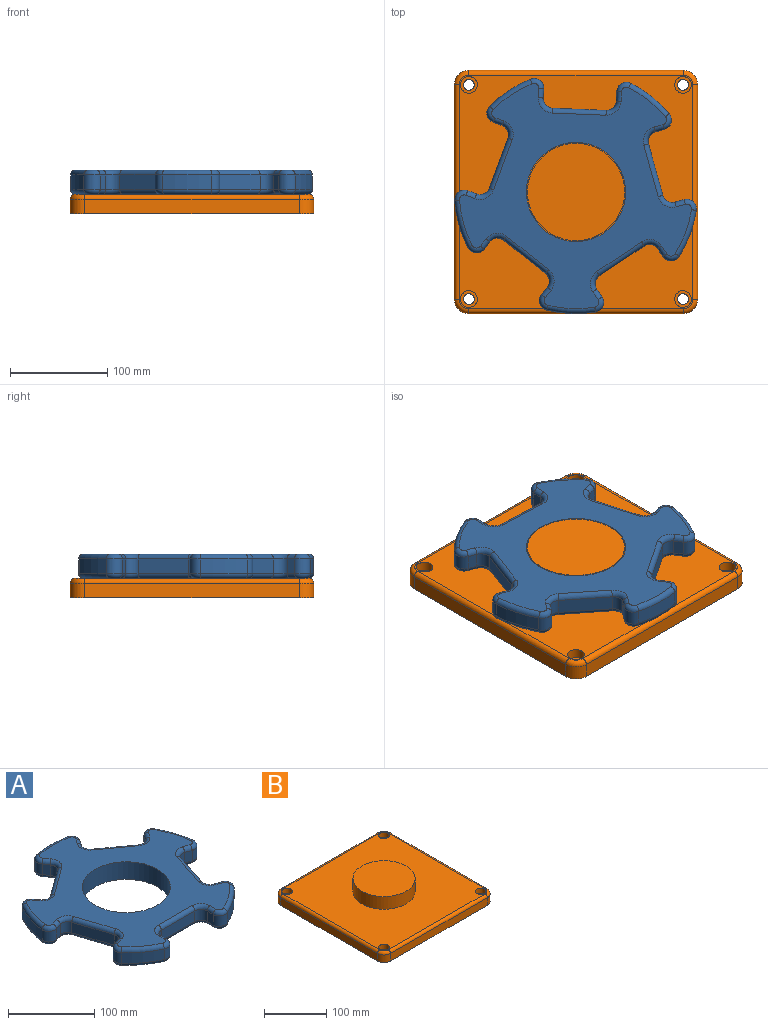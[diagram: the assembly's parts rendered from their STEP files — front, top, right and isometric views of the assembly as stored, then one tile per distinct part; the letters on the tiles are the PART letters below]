
ASSEMBLY  parts=2 mates=1
PART A: 123 faces, bbox 268.9x258.5x25 mm
  f0: plane 238.57x229.73mm, normal (0,0,1), area 21505.7mm2, adj f6,f43,f44,f45,f46,f47,f48,f49
  f1: plane 238.57x229.73mm, normal (0,0,-1), area 21505.7mm2, adj f6,f83,f84,f85,f86,f87,f88,f89
  f2: cylinder r=125mm len=40.68mm, axis (0,0,-1), area 759.5mm2, adj f13,f42,f51,f91
  f3: cylinder r=125mm len=47.82mm, axis (0,0,-1), area 759.5mm2, adj f35,f41,f67,f107
  f4: cylinder r=125mm len=50.29mm, axis (0,0,-1), area 759.5mm2, adj f28,f34,f82,f122
  f5: cylinder r=125mm len=47.82mm, axis (0,0,-1), area 759.5mm2, adj f21,f27,f66,f106
  f6: cylinder r=51mm len=102mm, axis (0,0,-1), area 8011.1mm2, adj f0,f1
  f7: cylinder r=125mm len=40.68mm, axis (0,0,-1), area 759.5mm2, adj f14,f20,f50,f90
  f8: plane 15x9.73mm, normal (-1,0,0), area 146mm2, adj f11,f14,f46,f86
  f9: plane 55x15mm, normal (0,-1,0), area 825mm2, adj f11,f12,f43,f83
  f10: plane 15x9.73mm, normal (1,0,0), area 146mm2, adj f12,f13,f47,f87
  f11: cylinder r=10mm len=15mm, axis (0,0,-1), area 235.6mm2, adj f8,f9,f44,f84
  f12: cylinder r=10mm len=15mm, axis (0,0,-1), area 235.6mm2, adj f9,f10,f45,f85
  f13: cylinder r=10mm len=15mm, axis (0,0,-1), area 299.5mm2, adj f2,f10,f49,f89
  f14: cylinder r=10mm len=15mm, axis (0,0,-1), area 299.5mm2, adj f7,f8,f48,f88
  f15: plane 15x9.26mm, normal (-0.31,-0.95,0), area 146mm2, adj f18,f21,f62,f102
  f16: plane 52.31x17mm, normal (0.95,-0.31,0), area 825mm2, adj f18,f19,f58,f98
  f17: plane 15x9.26mm, normal (0.31,0.95,0), area 146mm2, adj f19,f20,f54,f94
  f18: cylinder r=10mm len=15mm, axis (0,0,-1), area 235.6mm2, adj f15,f16,f60,f100
  f19: cylinder r=10mm len=15mm, axis (0,0,-1), area 235.6mm2, adj f16,f17,f56,f96
  f20: cylinder r=10mm len=16.25mm, axis (0,0,-1), area 299.5mm2, adj f7,f17,f52,f92
  f21: cylinder r=10mm len=15mm, axis (0,0,-1), area 299.5mm2, adj f5,f15,f64,f104
  f22: plane 15x7.87mm, normal (0.81,-0.59,0), area 146mm2, adj f25,f28,f78,f118
  f23: plane 44.5x32.33mm, normal (0.59,0.81,0), area 825mm2, adj f25,f26,f74,f114
  f24: plane 15x7.87mm, normal (-0.81,0.59,0), area 146mm2, adj f26,f27,f70,f110
  f25: cylinder r=10mm len=15mm, axis (0,0,-1), area 235.6mm2, adj f22,f23,f76,f116
  f26: cylinder r=10mm len=15mm, axis (0,0,-1), area 235.6mm2, adj f23,f24,f72,f112
  f27: cylinder r=10mm len=16.78mm, axis (0,0,-1), area 299.5mm2, adj f5,f24,f68,f108
  f28: cylinder r=10mm len=15.67mm, axis (0,0,-1), area 299.5mm2, adj f4,f22,f80,f120
  f29: plane 15x7.87mm, normal (0.81,0.59,0), area 146mm2, adj f32,f35,f71,f111
  f30: plane 44.5x32.33mm, normal (-0.59,0.81,0), area 825mm2, adj f32,f33,f75,f115
  f31: plane 15x7.87mm, normal (-0.81,-0.59,0), area 146mm2, adj f33,f34,f79,f119
  f32: cylinder r=10mm len=15mm, axis (0,0,-1), area 235.6mm2, adj f29,f30,f73,f113
  f33: cylinder r=10mm len=15mm, axis (0,0,-1), area 235.6mm2, adj f30,f31,f77,f117
  f34: cylinder r=10mm len=15.67mm, axis (0,0,-1), area 299.5mm2, adj f4,f31,f81,f121
  f35: cylinder r=10mm len=16.78mm, axis (0,0,-1), area 299.5mm2, adj f3,f29,f69,f109
  f36: plane 15x9.26mm, normal (-0.31,0.95,0), area 146mm2, adj f39,f42,f55,f95
  f37: plane 52.31x17mm, normal (-0.95,-0.31,0), area 825mm2, adj f39,f40,f59,f99
  f38: plane 15x9.26mm, normal (0.31,-0.95,0), area 146mm2, adj f40,f41,f63,f103
  f39: cylinder r=10mm len=15mm, axis (0,0,-1), area 235.6mm2, adj f36,f37,f57,f97
  f40: cylinder r=10mm len=15mm, axis (0,0,-1), area 235.6mm2, adj f37,f38,f61,f101
  f41: cylinder r=10mm len=15mm, axis (0,0,-1), area 299.5mm2, adj f3,f38,f65,f105
  f42: cylinder r=10mm len=16.25mm, axis (0,0,-1), area 299.5mm2, adj f2,f36,f53,f93
  f43: cylinder r=5mm len=55mm, axis (1,0,0), area 432mm2, adj f0,f9,f44,f45
  f44: torus R=15mm, axis (0,0,1), area 145.8mm2, adj f0,f11,f43,f46
  f45: torus R=15mm, axis (0,0,1), area 145.8mm2, adj f0,f12,f43,f47
  f46: cylinder r=5mm len=9.73mm, axis (0,-1,0), area 76.4mm2, adj f0,f8,f44,f48
  f47: cylinder r=5mm len=9.73mm, axis (0,1,0), area 76.4mm2, adj f0,f10,f45,f49
  f48: torus R=5mm, axis (0,0,1), area 128.3mm2, adj f0,f14,f46,f50
  f49: torus R=5mm, axis (0,0,1), area 128.3mm2, adj f0,f13,f47,f51
  f50: torus R=120mm, axis (0,0,1), area 391.9mm2, adj f0,f7,f48,f52
  f51: torus R=120mm, axis (0,0,1), area 391.9mm2, adj f0,f2,f49,f53
  f52: torus R=5mm, axis (0,0,1), area 128.3mm2, adj f0,f20,f50,f54
  f53: torus R=5mm, axis (0,0,1), area 128.3mm2, adj f0,f42,f51,f55
  f54: cylinder r=5mm len=10.8mm, axis (-0.95,0.31,0), area 76.4mm2, adj f0,f17,f52,f56
  f55: cylinder r=5mm len=10.8mm, axis (-0.95,-0.31,0), area 76.4mm2, adj f0,f36,f53,f57
  f56: torus R=15mm, axis (0,0,1), area 145.8mm2, adj f0,f19,f54,f58
  f57: torus R=15mm, axis (0,0,1), area 145.8mm2, adj f0,f39,f55,f59
  f58: cylinder r=5mm len=53.85mm, axis (0.31,0.95,0), area 432mm2, adj f0,f16,f56,f60
  f59: cylinder r=5mm len=53.85mm, axis (0.31,-0.95,0), area 432mm2, adj f0,f37,f57,f61
  f60: torus R=15mm, axis (0,0,1), area 145.8mm2, adj f0,f18,f58,f62
  f61: torus R=15mm, axis (0,0,1), area 145.8mm2, adj f0,f40,f59,f63
  f62: cylinder r=5mm len=10.8mm, axis (0.95,-0.31,0), area 76.4mm2, adj f0,f15,f60,f64
  f63: cylinder r=5mm len=10.8mm, axis (0.95,0.31,0), area 76.4mm2, adj f0,f38,f61,f65
  f64: torus R=5mm, axis (0,0,1), area 128.3mm2, adj f0,f21,f62,f66
  f65: torus R=5mm, axis (0,0,1), area 128.3mm2, adj f0,f41,f63,f67
  f66: torus R=120mm, axis (0,0,1), area 391.9mm2, adj f0,f5,f64,f68
  f67: torus R=120mm, axis (0,0,1), area 391.9mm2, adj f0,f3,f65,f69
  f68: torus R=5mm, axis (0,0,1), area 128.3mm2, adj f0,f27,f66,f70
  f69: torus R=5mm, axis (0,0,1), area 128.3mm2, adj f0,f35,f67,f71
  f70: cylinder r=5mm len=10.81mm, axis (-0.59,-0.81,0), area 76.4mm2, adj f0,f24,f68,f72
  f71: cylinder r=5mm len=10.81mm, axis (-0.59,0.81,0), area 76.4mm2, adj f0,f29,f69,f73
  f72: torus R=15mm, axis (0,0,1), area 145.8mm2, adj f0,f26,f70,f74
  f73: torus R=15mm, axis (0,0,1), area 145.8mm2, adj f0,f32,f71,f75
  f74: cylinder r=5mm len=47.44mm, axis (-0.81,0.59,0), area 432mm2, adj f0,f23,f72,f76
  f75: cylinder r=5mm len=47.44mm, axis (-0.81,-0.59,0), area 432mm2, adj f0,f30,f73,f77
  f76: torus R=15mm, axis (0,0,1), area 145.8mm2, adj f0,f25,f74,f78
  f77: torus R=15mm, axis (0,0,1), area 145.8mm2, adj f0,f33,f75,f79
  f78: cylinder r=5mm len=10.81mm, axis (0.59,0.81,0), area 76.4mm2, adj f0,f22,f76,f80
  f79: cylinder r=5mm len=10.81mm, axis (0.59,-0.81,0), area 76.4mm2, adj f0,f31,f77,f81
  f80: torus R=5mm, axis (0,0,1), area 128.3mm2, adj f0,f28,f78,f82
  f81: torus R=5mm, axis (0,0,1), area 128.3mm2, adj f0,f34,f79,f82
  f82: torus R=120mm, axis (0,0,1), area 391.9mm2, adj f0,f4,f80,f81
  f83: cylinder r=5mm len=55mm, axis (-1,0,0), area 432mm2, adj f1,f9,f84,f85
  f84: torus R=15mm, axis (0,0,1), area 145.8mm2, adj f1,f11,f83,f86
  f85: torus R=15mm, axis (0,0,1), area 145.8mm2, adj f1,f12,f83,f87
  f86: cylinder r=5mm len=9.73mm, axis (0,1,0), area 76.4mm2, adj f1,f8,f84,f88
  f87: cylinder r=5mm len=9.73mm, axis (0,-1,0), area 76.4mm2, adj f1,f10,f85,f89
  f88: torus R=5mm, axis (0,0,1), area 128.3mm2, adj f1,f14,f86,f90
  f89: torus R=5mm, axis (0,0,1), area 128.3mm2, adj f1,f13,f87,f91
  f90: torus R=120mm, axis (0,0,1), area 391.9mm2, adj f1,f7,f88,f92
  f91: torus R=120mm, axis (0,0,1), area 391.9mm2, adj f1,f2,f89,f93
  f92: torus R=5mm, axis (0,0,1), area 128.3mm2, adj f1,f20,f90,f94
  f93: torus R=5mm, axis (0,0,1), area 128.3mm2, adj f1,f42,f91,f95
  f94: cylinder r=5mm len=10.8mm, axis (0.95,-0.31,0), area 76.4mm2, adj f1,f17,f92,f96
  f95: cylinder r=5mm len=10.8mm, axis (0.95,0.31,0), area 76.4mm2, adj f1,f36,f93,f97
  f96: torus R=15mm, axis (0,0,1), area 145.8mm2, adj f1,f19,f94,f98
  f97: torus R=15mm, axis (0,0,1), area 145.8mm2, adj f1,f39,f95,f99
  f98: cylinder r=5mm len=53.85mm, axis (-0.31,-0.95,0), area 432mm2, adj f1,f16,f96,f100
  f99: cylinder r=5mm len=53.85mm, axis (-0.31,0.95,0), area 432mm2, adj f1,f37,f97,f101
  f100: torus R=15mm, axis (0,0,1), area 145.8mm2, adj f1,f18,f98,f102
  f101: torus R=15mm, axis (0,0,1), area 145.8mm2, adj f1,f40,f99,f103
  f102: cylinder r=5mm len=10.8mm, axis (-0.95,0.31,0), area 76.4mm2, adj f1,f15,f100,f104
  f103: cylinder r=5mm len=10.8mm, axis (-0.95,-0.31,0), area 76.4mm2, adj f1,f38,f101,f105
  f104: torus R=5mm, axis (0,0,1), area 128.3mm2, adj f1,f21,f102,f106
  f105: torus R=5mm, axis (0,0,1), area 128.3mm2, adj f1,f41,f103,f107
  f106: torus R=120mm, axis (0,0,1), area 391.9mm2, adj f1,f5,f104,f108
  f107: torus R=120mm, axis (0,0,1), area 391.9mm2, adj f1,f3,f105,f109
  f108: torus R=5mm, axis (0,0,1), area 128.3mm2, adj f1,f27,f106,f110
  f109: torus R=5mm, axis (0,0,1), area 128.3mm2, adj f1,f35,f107,f111
  f110: cylinder r=5mm len=10.81mm, axis (0.59,0.81,0), area 76.4mm2, adj f1,f24,f108,f112
  f111: cylinder r=5mm len=10.81mm, axis (0.59,-0.81,0), area 76.4mm2, adj f1,f29,f109,f113
  f112: torus R=15mm, axis (0,0,1), area 145.8mm2, adj f1,f26,f110,f114
  f113: torus R=15mm, axis (0,0,1), area 145.8mm2, adj f1,f32,f111,f115
  f114: cylinder r=5mm len=47.44mm, axis (0.81,-0.59,0), area 432mm2, adj f1,f23,f112,f116
  f115: cylinder r=5mm len=47.44mm, axis (0.81,0.59,0), area 432mm2, adj f1,f30,f113,f117
  f116: torus R=15mm, axis (0,0,1), area 145.8mm2, adj f1,f25,f114,f118
  f117: torus R=15mm, axis (0,0,1), area 145.8mm2, adj f1,f33,f115,f119
  f118: cylinder r=5mm len=10.81mm, axis (-0.59,-0.81,0), area 76.4mm2, adj f1,f22,f116,f120
  f119: cylinder r=5mm len=10.81mm, axis (-0.59,0.81,0), area 76.4mm2, adj f1,f31,f117,f121
  f120: torus R=5mm, axis (0,0,1), area 128.3mm2, adj f1,f28,f118,f122
  f121: torus R=5mm, axis (0,0,1), area 128.3mm2, adj f1,f34,f119,f122
  f122: torus R=120mm, axis (0,0,1), area 391.9mm2, adj f1,f4,f120,f121
PART B: 32 faces, bbox 252.5x252.5x45 mm
  f0: plane 220x15mm, normal (1,0,0), area 3300mm2, adj f5,f8,f11,f27
  f1: plane 220x15mm, normal (0,1,0), area 3300mm2, adj f5,f8,f9,f31
  f2: plane 220x15mm, normal (-1,0,0), area 3300mm2, adj f5,f9,f10,f28
  f3: plane 220x15mm, normal (0,-1,0), area 3300mm2, adj f5,f10,f11,f24
  f4: plane 240x240mm, normal (0,0,1), area 48725.4mm2, adj f6,f14,f17,f20,f23,f24,f25,f26
  f5: plane 250x250mm, normal (0,0,-1), area 61926.7mm2, adj f0,f1,f2,f3,f8,f9,f10,f11
  f6: cylinder r=50mm len=100mm, axis (0,0,-1), area 7854mm2, adj f4,f7
  f7: plane 100x100mm, normal (0,0,1), area 7854mm2, adj f6
  f8: cylinder r=15mm len=15mm, axis (0,0,-1), area 353.4mm2, adj f0,f1,f5,f29
  f9: cylinder r=15mm len=15mm, axis (0,0,1), area 353.4mm2, adj f1,f2,f5,f30
  f10: cylinder r=15mm len=15mm, axis (0,0,-1), area 353.4mm2, adj f2,f3,f5,f26
  f11: cylinder r=15mm len=15mm, axis (0,0,1), area 353.4mm2, adj f0,f3,f5,f25
  f12: cylinder r=5.5mm len=11mm, axis (0,0,1), area 345.6mm2, adj f5,f13
  f13: plane 17.25x17.25mm, normal (0,0,1), area 138.7mm2, adj f12,f14
  f14: cylinder r=8.62mm len=17.25mm, axis (0,0,1), area 541.9mm2, adj f4,f13
  f15: cylinder r=5.5mm len=11mm, axis (0,0,1), area 345.6mm2, adj f5,f16
  f16: plane 17.25x17.25mm, normal (0,0,1), area 138.7mm2, adj f15,f17
  f17: cylinder r=8.62mm len=17.25mm, axis (0,0,1), area 541.9mm2, adj f4,f16
  f18: cylinder r=5.5mm len=11mm, axis (0,0,1), area 345.6mm2, adj f5,f19
  f19: plane 17.25x17.25mm, normal (0,0,1), area 138.7mm2, adj f18,f20
  f20: cylinder r=8.62mm len=17.25mm, axis (0,0,1), area 541.9mm2, adj f4,f19
  f21: cylinder r=5.5mm len=11mm, axis (0,0,1), area 345.6mm2, adj f5,f22
  f22: plane 17.25x17.25mm, normal (0,0,1), area 138.7mm2, adj f21,f23
  f23: cylinder r=8.62mm len=17.25mm, axis (0,0,1), area 541.9mm2, adj f4,f22
  f24: cylinder r=5mm len=220mm, axis (-1,0,0), area 1727.9mm2, adj f3,f4,f25,f26
  f25: torus R=10mm, axis (0,0,1), area 162.6mm2, adj f4,f11,f24,f27
  f26: torus R=10mm, axis (0,0,1), area 162.6mm2, adj f4,f10,f24,f28
  f27: cylinder r=5mm len=220mm, axis (0,-1,0), area 1727.9mm2, adj f0,f4,f25,f29
  f28: cylinder r=5mm len=220mm, axis (0,1,0), area 1727.9mm2, adj f2,f4,f26,f30
  f29: torus R=10mm, axis (0,0,1), area 162.6mm2, adj f4,f8,f27,f31
  f30: torus R=10mm, axis (0,0,1), area 162.6mm2, adj f4,f9,f28,f31
  f31: cylinder r=5mm len=220mm, axis (1,0,0), area 1727.9mm2, adj f1,f4,f29,f30
PLACE A rot(axis=(0,0,1),105.6deg) t=(0,0,0)mm
PLACE B at identity fixed
MATE revolute A.f2 <-> B.f6  axis (0,0,-1) through (0,0,32.5)mm
